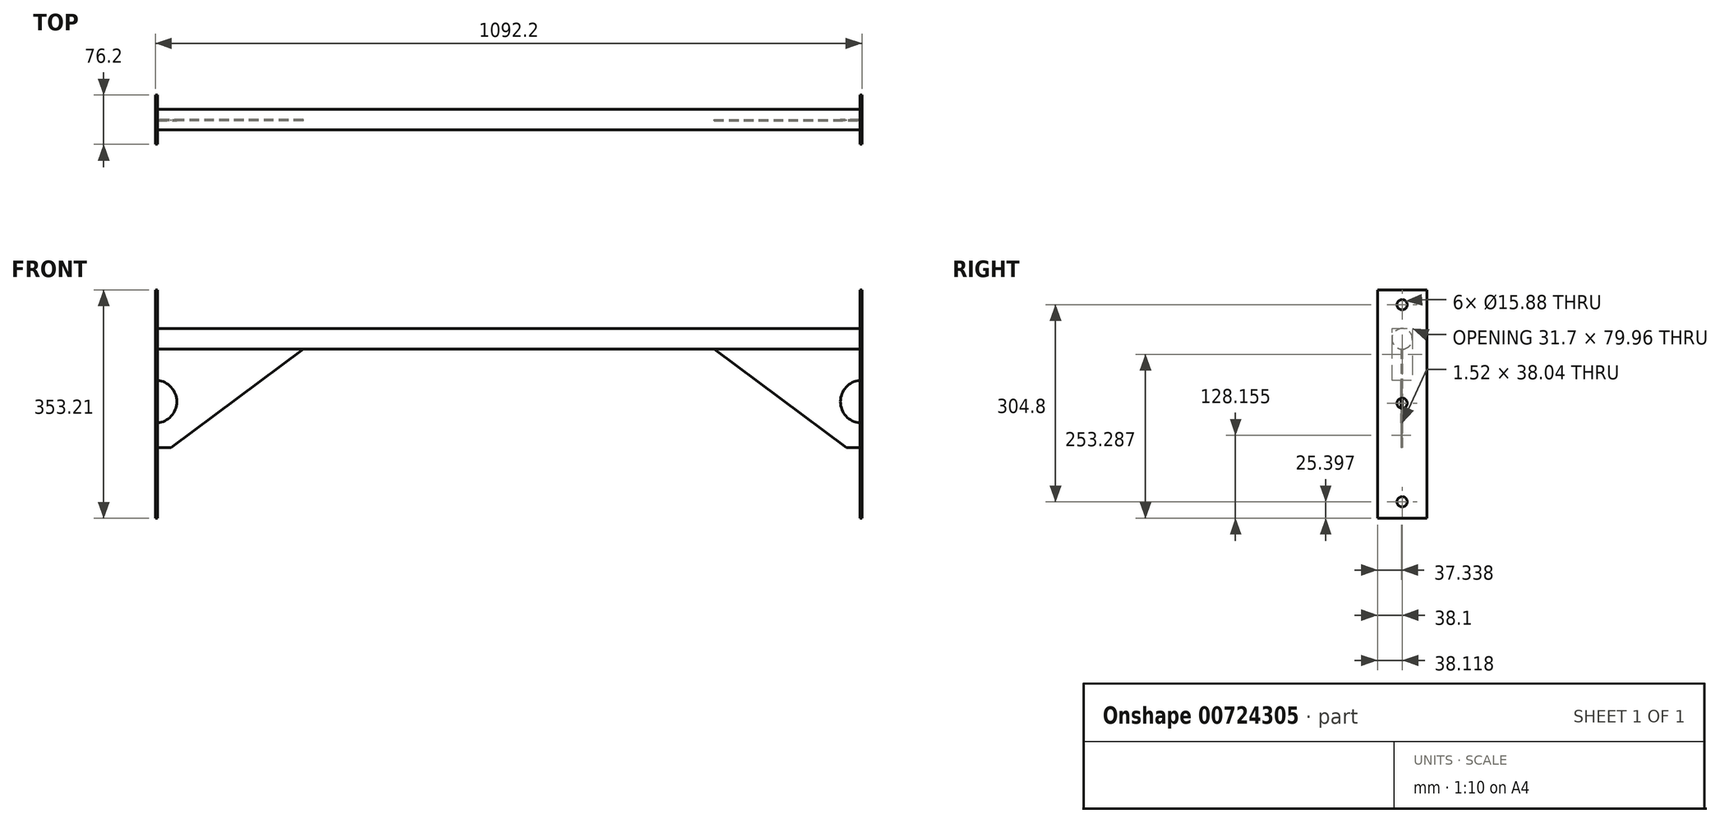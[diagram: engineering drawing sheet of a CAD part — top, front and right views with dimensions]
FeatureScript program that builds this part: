
annotation { "Feature Type Name" : "Feature", "Feature Type Description" : "" }
export const myFeature = defineFeature(function(context is Context, id is Id, definition is map)
    precondition{}
    {
        {
            var Q0;
            Q0=qCreatedBy(makeId("Right.planeOp"),FACE);
            var sketch = newSketch(context, id + "F0", { "sketchPlane" : qUnion([Q0])});
            skLineSegment(sketch, "E0.bottom", {"start": v(38.1, 75.8) * mm, "end": v(-38.1, 75.8) * mm});
            skLineSegment(sketch, "E0.top", {"start": v(38.1, -277.41) * mm, "end": v(-38.1, -277.41) * mm});
            skLineSegment(sketch, "E0.left", {"start": v(38.1, 75.8) * mm, "end": v(38.1, -277.41) * mm});
            skLineSegment(sketch, "E0.right", {"start": v(-38.1, 75.8) * mm, "end": v(-38.1, -277.41) * mm});
            skCircle(sketch, "E1", {"center": v(0, -252.01) * mm, "radius": 7.94 * mm});
            skCircle(sketch, "E2", {"center": v(0, -99.61) * mm, "radius": 7.94 * mm});
            skCircle(sketch, "E3", {"center": v(0, 52.79) * mm, "radius": 7.94 * mm});
            skCircle(sketch, "E4", {"center": v(0, 0) * mm, "radius": 15.88 * mm});
            skSolve(sketch);
        }
        {
            var Q0;
            Q0=makeQuery(id+"F0.imprint","IMPRINT",FACE,{"disambiguationData":[TD([[makeQuery(id+"F0.imprint","IMPRINT",EDGE,{"derivedFrom":sQuery(id+"F0.wireOp",EDGE,"E4")}),1.0]])]});
            extrude(context, id + "F1", {"entities" : qUnion([Q0]), "depth" : 1092.2 * mm, "offsetDistance" : 25.4 * mm});
        }
        {
            var Q0;
            Q0=qCreatedBy(makeId("Front.planeOp"),FACE);
            var sketch = newSketch(context, id + "F2", { "sketchPlane" : qUnion([Q0])});
            skLineSegment(sketch, "E5.bottom", {"start": v(0, 0) * mm, "end": v(228.6, 0) * mm});
            skLineSegment(sketch, "E5.left", {"start": v(0, 0) * mm, "end": v(0, -168.28) * mm});
            skLineSegment(sketch, "E6", {"start": v(228.6, -16.08) * mm, "end": v(24, -168.28) * mm});
            skLineSegment(sketch, "E7", {"start": v(0, -168.28) * mm, "end": v(24, -168.28) * mm});
            skLineSegment(sketch, "E8", {"start": v(228.6, 0) * mm, "end": v(228.6, -16.08) * mm});
            skArc(sketch, "E9", {"start": v(0, -130.38) * mm, "mid": v(33.2, -97.17) * mm, "end": v(0, -63.96) * mm});
            skSolve(sketch);
        }
        {
            var Q0;
            Q0=qCreatedBy(makeId("Right.planeOp"),FACE);
            cPlane(context, id + "F3", {"entities" : qUnion([Q0]), "cplaneType" : CPlaneType.OFFSET, "offset" : 546.1 * mm, "width" : 152.4 * mm, "height" : 152.4 * mm});
        }
        {
            var Q0;
            Q0=makeQuery(id+"F0.imprint","IMPRINT",FACE,{"disambiguationData":[TD([[makeQuery(id+"F0.imprint","IMPRINT",EDGE,{"derivedFrom":sQuery(id+"F0.wireOp",EDGE,"E0.bottom")}),1.0]])]});
            extrude(context, id + "F4", {"entities" : qUnion([Q0]), "operationType" : NewBodyOperationType.ADD, "depth" : 3.05 * mm, "offsetDistance" : 25.4 * mm});
        }
        {
            var Q0;
            {var subQ3=sQuery(id+"F2.wireOp",EDGE,"E5.bottom");Q0=makeQuery(id+"F2.imprint","IMPRINT",FACE,{"disambiguationData":[TD([[makeQuery(id+"F2.imprint","IMPRINT",EDGE,{"derivedFrom":subQ3}),-1.0]])]});}
            extrude(context, id + "F5", {"entities" : qUnion([Q0]), "operationType" : NewBodyOperationType.ADD, "depth" : 1.52 * mm, "offsetDistance" : 25.4 * mm});
        }
        {
            var Q0;
            {var subQ3=sQuery(id+"F2.wireOp",EDGE,"E5.bottom");Q0=makeQuery(id+"F2.imprint","IMPRINT",FACE,{"disambiguationData":[TD([[makeQuery(id+"F2.imprint","IMPRINT",EDGE,{"derivedFrom":subQ3}),-1.0]])]});}
            extrude(context, id + "F6", {"entities" : qUnion([Q0]), "operationType" : NewBodyOperationType.ADD, "depth" : 1.52 * mm, "offsetDistance" : 25.4 * mm});
        }
        {
            var Q0;
            Q0=makeQuery(id+"F1.opExtrude","SWEPT_BODY",BODY,{"disambiguationData":[OSD([sQuery(id+"F0.wireOp",EDGE,"E4")])]});
            var Q1;
            Q1=qCreatedBy(id+"F3.planeOp",FACE);
            mirror(context, id + "F7", {"operationType" : NewBodyOperationType.ADD, "entities" : qUnion([Q0]), "mirrorPlane" : qUnion([Q1])});
        }
    });
